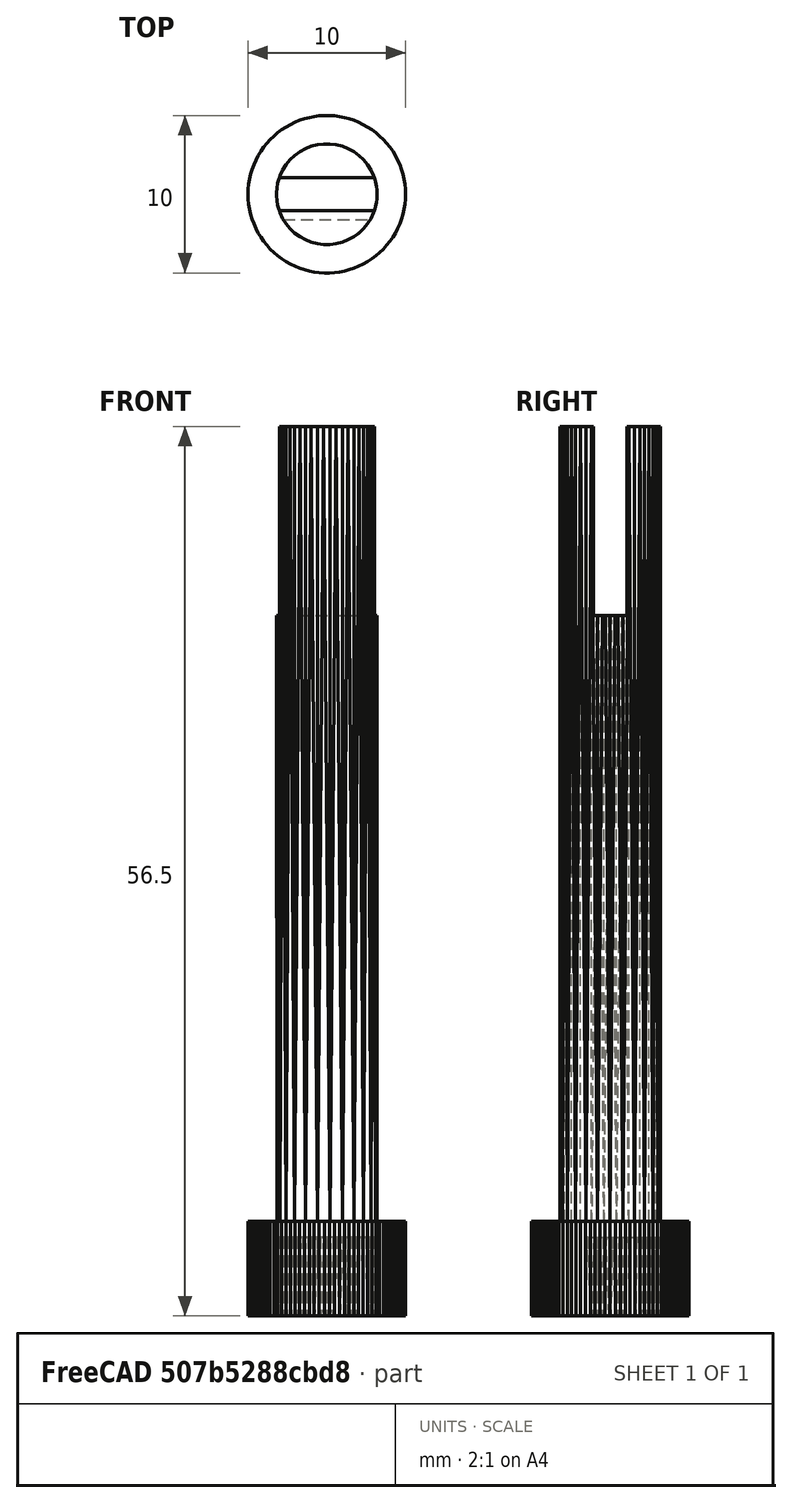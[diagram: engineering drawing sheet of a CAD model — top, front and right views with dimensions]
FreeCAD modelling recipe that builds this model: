
FCSTD DOCUMENT  (FreeCAD 0.17R13522 (Git))
Label: v5_bastago_largo
License: CreativeCommons Attribution-ShareAlike
LicenseURL: http://creativecommons.org/licenses/by-sa/4.0/
objects: Part::Box×2, Part::Cut×2, Part::Feature×1
note: 5 computed .brp shape members not serialized (recipe doc carries the construction recipe); baked Part::Feature solids carry a one-line shape summary decoded from their .brp

FEATURE [Part::Feature] bastago_largo001_solid001  label="bastago_largo001 (Solid)001"
  shape: bbox 10 x 9.995 x 58.5 mm, 275 faces (baked)
FEATURE [Part::Box] Box  label="Cube"
  AttacherType = Attacher::AttachEngine3D
  Height = 10
  Length = 15
  Placement = pos=(-7,-8,-8) rot=(0,0,1;0rad)
  Width = 15
FEATURE [Part::Cut] Cut
  Base = -> bastago_largo001_solid001
  Refine = true
  Tool = -> Box
FEATURE [Part::Box] Box001  label="Cube001"
  AttacherType = Attacher::AttachEngine3D
  Height = 12
  Length = 10
  Placement = pos=(-5,-1.05,46.5) rot=(0,0,1;0rad)
  Width = 2.1
FEATURE [Part::Cut] Cut001  label="bastago con encastres"
  Base = -> Cut
  Refine = true
  Tool = -> Box001
